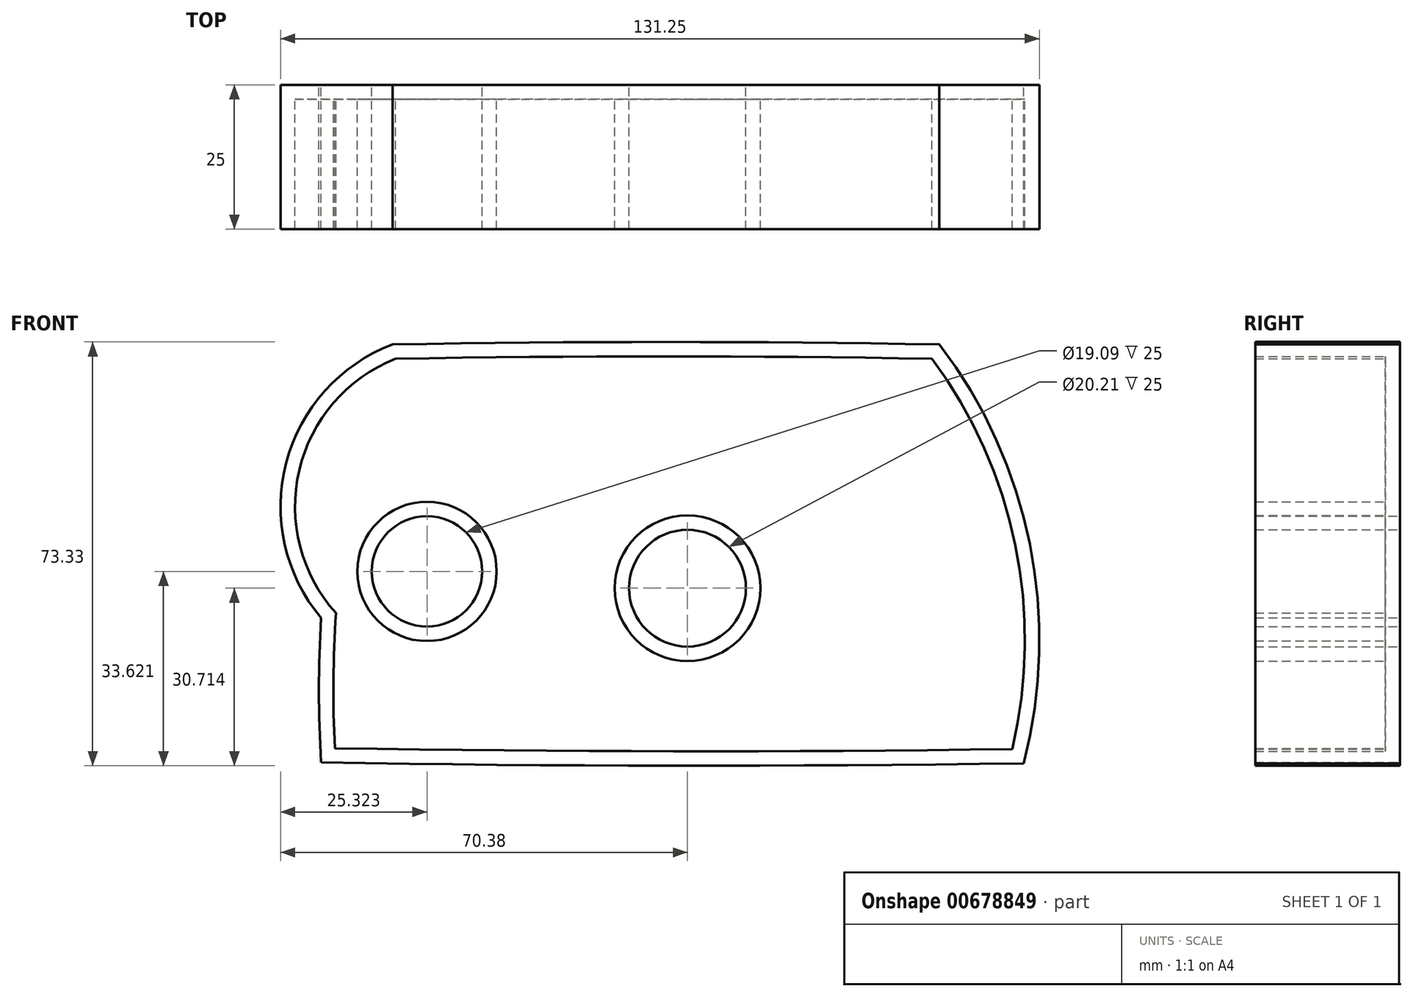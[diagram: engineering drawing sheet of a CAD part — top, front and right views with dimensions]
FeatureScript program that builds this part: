
annotation { "Feature Type Name" : "Feature", "Feature Type Description" : "" }
export const myFeature = defineFeature(function(context is Context, id is Id, definition is map)
    precondition{}
    {
        {
            var Q0;
            Q0=qCreatedBy(makeId("Front.planeOp"),FACE);
            var sketch = newSketch(context, id + "F0", { "sketchPlane" : qUnion([Q0])});
            skArc(sketch, "E0", {"start": v(58.12, -20.13) * mm, "mid": v(59.22, 17.8) * mm, "end": v(43.57, 52.36) * mm});
            skArc(sketch, "E1", {"start": v(43.57, 52.36) * mm, "mid": v(-3.72, 52.79) * mm, "end": v(-51.02, 52.36) * mm});
            skArc(sketch, "E2", {"start": v(-51.02, 52.36) * mm, "mid": v(-69.4, 31.88) * mm, "end": v(-63.37, 5.03) * mm});
            skArc(sketch, "E3", {"start": v(-63.37, 5.03) * mm, "mid": v(-63.74, -7.47) * mm, "end": v(-63.37, -19.97) * mm});
            skArc(sketch, "E4", {"start": v(-63.37, -19.97) * mm, "mid": v(-2.63, -20.54) * mm, "end": v(58.12, -20.13) * mm});
            skCircle(sketch, "E5", {"center": v(-45.06, 13.08) * mm, "radius": 9.55 * mm});
            skCircle(sketch, "E6", {"center": v(0, 10.17) * mm, "radius": 10.1 * mm});
            skSolve(sketch);
        }
        {
            var Q0;
            Q0=makeQuery(id+"F0.imprint","IMPRINT",FACE,{"disambiguationData":[TD([[makeQuery(id+"F0.imprint","IMPRINT",EDGE,{"derivedFrom":sQuery(id+"F0.wireOp",EDGE,"E0")}),1.0]])]});
            extrude(context, id + "F1", {"entities" : qUnion([Q0]), "depth" : 25 * mm, "offsetDistance" : 25 * mm});
        }
        {
            var Q0;
            Q0=makeQuery(id+"F1.opExtrude","CAP_FACE",FACE,{"disambiguationData":[OSD([sQuery(id+"F0.wireOp",EDGE,"E0"),sQuery(id+"F0.wireOp",EDGE,"E1"),sQuery(id+"F0.wireOp",EDGE,"E2"),sQuery(id+"F0.wireOp",EDGE,"E3"),sQuery(id+"F0.wireOp",EDGE,"E4")])],"isStart":false});
            shell(context, id + "F2", {"entities" : qUnion([Q0]), "thickness" : 2.5 * mm});
        }
    });
